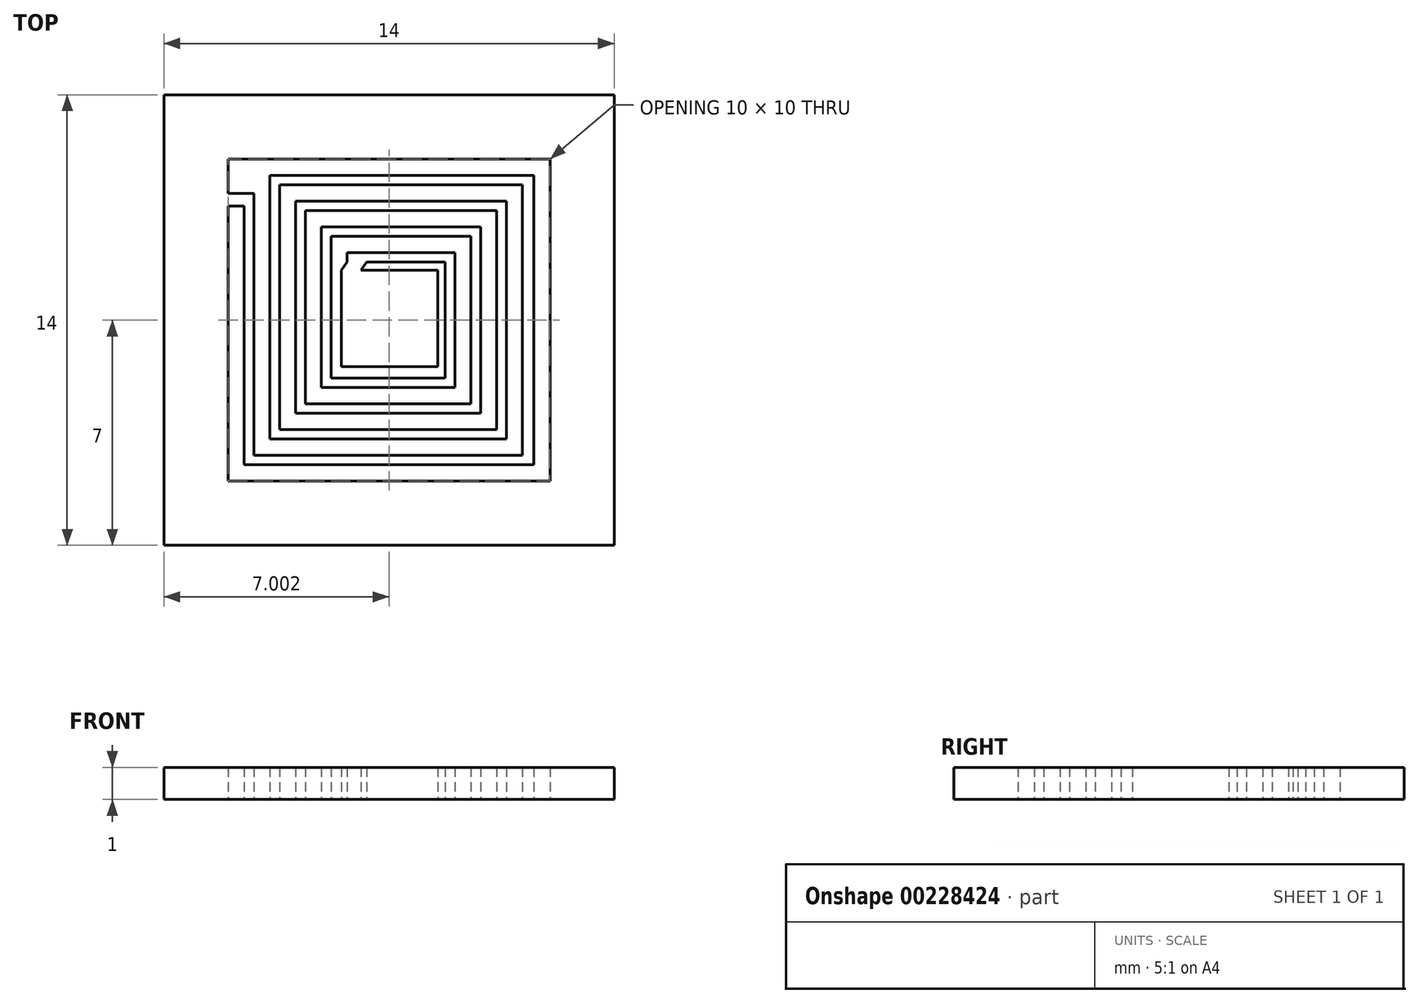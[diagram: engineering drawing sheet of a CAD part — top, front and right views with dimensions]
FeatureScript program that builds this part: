
annotation { "Feature Type Name" : "Feature", "Feature Type Description" : "" }
export const myFeature = defineFeature(function(context is Context, id is Id, definition is map)
    precondition{}
    {
        {
            var Q0;
            Q0=qCreatedBy(makeId("Top.planeOp"),FACE);
            var sketch = newSketch(context, id + "F0", { "sketchPlane" : qUnion([Q0])});
            skLineSegment(sketch, "E0.bottom", {"start": v(-33.55, 10) * mm, "end": v(-23.55, 10) * mm});
            skLineSegment(sketch, "E0.top", {"start": v(-33.55, 0) * mm, "end": v(-23.55, 0) * mm});
            skLineSegment(sketch, "E0.left", {"start": v(-33.55, 10) * mm, "end": v(-33.55, 0) * mm});
            skLineSegment(sketch, "E0.right", {"start": v(-23.55, 10) * mm, "end": v(-23.55, 0) * mm});
            skLineSegment(sketch, "E1.bottom", {"start": v(-29.42, 6.55) * mm, "end": v(-27.03, 6.55) * mm});
            skLineSegment(sketch, "E1.top", {"start": v(-30.03, 3.55) * mm, "end": v(-27.03, 3.55) * mm});
            skLineSegment(sketch, "E1.left", {"start": v(-30.03, 6.55) * mm, "end": v(-30.03, 3.55) * mm});
            skLineSegment(sketch, "E1.right", {"start": v(-27.03, 6.55) * mm, "end": v(-27.03, 3.55) * mm});
            skLineSegment(sketch, "E2.bottom", {"start": v(-33.05, 8.94) * mm, "end": v(-32.75, 8.94) * mm});
            skLineSegment(sketch, "E2.left", {"start": v(-33.05, 8.54) * mm, "end": v(-33.05, 0.8) * mm});
            skLineSegment(sketch, "E2.right", {"start": v(-32.75, 8.94) * mm, "end": v(-32.75, 0.8) * mm});
            skLineSegment(sketch, "E3", {"start": v(-33.05, 8.94) * mm, "end": v(-33.55, 8.94) * mm});
            skLineSegment(sketch, "E4", {"start": v(-33.55, 8.54) * mm, "end": v(-33.05, 8.54) * mm});
            skLineSegment(sketch, "E5.bottom", {"start": v(-32.75, 0.8) * mm, "end": v(-24.4, 0.8) * mm});
            skLineSegment(sketch, "E5.top", {"start": v(-33.05, 0.5) * mm, "end": v(-24.05, 0.5) * mm});
            skLineSegment(sketch, "E5.left", {"start": v(-33.05, 0.8) * mm, "end": v(-33.05, 0.5) * mm});
            skLineSegment(sketch, "E5.right", {"start": v(-24.05, 0.8) * mm, "end": v(-24.05, 0.5) * mm});
            skLineSegment(sketch, "E6.top", {"start": v(-24.05, 9.5) * mm, "end": v(-24.4, 9.5) * mm});
            skLineSegment(sketch, "E6.left", {"start": v(-24.05, 0.8) * mm, "end": v(-24.05, 9.5) * mm});
            skLineSegment(sketch, "E6.right", {"start": v(-24.4, 0.8) * mm, "end": v(-24.4, 9.2) * mm});
            skLineSegment(sketch, "E7.bottom", {"start": v(-24.4, 9.5) * mm, "end": v(-32.25, 9.5) * mm});
            skLineSegment(sketch, "E7.top", {"start": v(-24.4, 9.2) * mm, "end": v(-31.95, 9.2) * mm});
            skLineSegment(sketch, "E7.right", {"start": v(-32.25, 9.5) * mm, "end": v(-32.25, 9.2) * mm});
            skLineSegment(sketch, "E8.top", {"start": v(-32.25, 1.3) * mm, "end": v(-31.95, 1.3) * mm});
            skLineSegment(sketch, "E8.left", {"start": v(-32.25, 9.2) * mm, "end": v(-32.25, 1.3) * mm});
            skLineSegment(sketch, "E8.right", {"start": v(-31.95, 9.2) * mm, "end": v(-31.95, 1.6) * mm});
            skLineSegment(sketch, "E9.bottom", {"start": v(-31.95, 1.3) * mm, "end": v(-24.9, 1.3) * mm});
            skLineSegment(sketch, "E9.top", {"start": v(-31.95, 1.6) * mm, "end": v(-25.2, 1.6) * mm});
            skLineSegment(sketch, "E9.right", {"start": v(-24.9, 1.3) * mm, "end": v(-24.9, 1.6) * mm});
            skLineSegment(sketch, "E10.top", {"start": v(-24.9, 8.7) * mm, "end": v(-25.2, 8.7) * mm});
            skLineSegment(sketch, "E10.left", {"start": v(-24.9, 1.6) * mm, "end": v(-24.9, 8.7) * mm});
            skLineSegment(sketch, "E10.right", {"start": v(-25.2, 1.6) * mm, "end": v(-25.2, 8.4) * mm});
            skLineSegment(sketch, "E11.bottom", {"start": v(-25.2, 8.7) * mm, "end": v(-31.45, 8.7) * mm});
            skLineSegment(sketch, "E11.top", {"start": v(-25.2, 8.4) * mm, "end": v(-31.15, 8.4) * mm});
            skLineSegment(sketch, "E11.right", {"start": v(-31.45, 8.7) * mm, "end": v(-31.45, 8.4) * mm});
            skLineSegment(sketch, "E12.top", {"start": v(-31.45, 2.1) * mm, "end": v(-31.15, 2.1) * mm});
            skLineSegment(sketch, "E12.left", {"start": v(-31.45, 8.4) * mm, "end": v(-31.45, 2.1) * mm});
            skLineSegment(sketch, "E12.right", {"start": v(-31.15, 8.4) * mm, "end": v(-31.15, 2.4) * mm});
            skLineSegment(sketch, "E13.bottom", {"start": v(-31.15, 2.1) * mm, "end": v(-25.7, 2.1) * mm});
            skLineSegment(sketch, "E13.top", {"start": v(-31.15, 2.4) * mm, "end": v(-26, 2.4) * mm});
            skLineSegment(sketch, "E13.right", {"start": v(-25.7, 2.1) * mm, "end": v(-25.7, 2.4) * mm});
            skLineSegment(sketch, "E14.top", {"start": v(-25.7, 7.9) * mm, "end": v(-26, 7.9) * mm});
            skLineSegment(sketch, "E14.left", {"start": v(-25.7, 2.4) * mm, "end": v(-25.7, 7.9) * mm});
            skLineSegment(sketch, "E14.right", {"start": v(-26, 2.4) * mm, "end": v(-26, 7.6) * mm});
            skLineSegment(sketch, "E15.bottom", {"start": v(-26, 7.9) * mm, "end": v(-30.65, 7.9) * mm});
            skLineSegment(sketch, "E15.top", {"start": v(-26, 7.6) * mm, "end": v(-30.35, 7.6) * mm});
            skLineSegment(sketch, "E15.right", {"start": v(-30.65, 7.9) * mm, "end": v(-30.65, 7.6) * mm});
            skLineSegment(sketch, "E16.top", {"start": v(-30.65, 2.9) * mm, "end": v(-30.35, 2.9) * mm});
            skLineSegment(sketch, "E16.left", {"start": v(-30.65, 7.6) * mm, "end": v(-30.65, 2.9) * mm});
            skLineSegment(sketch, "E16.right", {"start": v(-30.35, 7.6) * mm, "end": v(-30.35, 3.2) * mm});
            skLineSegment(sketch, "E17.bottom", {"start": v(-30.35, 2.9) * mm, "end": v(-26.5, 2.9) * mm});
            skLineSegment(sketch, "E17.top", {"start": v(-30.35, 3.2) * mm, "end": v(-26.8, 3.2) * mm});
            skLineSegment(sketch, "E17.right", {"start": v(-26.5, 2.9) * mm, "end": v(-26.5, 3.2) * mm});
            skLineSegment(sketch, "E18.top", {"start": v(-26.5, 7.1) * mm, "end": v(-26.8, 7.1) * mm});
            skLineSegment(sketch, "E18.left", {"start": v(-26.5, 3.2) * mm, "end": v(-26.5, 7.1) * mm});
            skLineSegment(sketch, "E18.right", {"start": v(-26.8, 3.2) * mm, "end": v(-26.8, 6.8) * mm});
            skLineSegment(sketch, "E19.bottom", {"start": v(-26.8, 7.1) * mm, "end": v(-29.85, 7.1) * mm});
            skLineSegment(sketch, "E19.top", {"start": v(-26.8, 6.8) * mm, "end": v(-29.25, 6.8) * mm});
            skLineSegment(sketch, "E19.right", {"start": v(-29.85, 7.1) * mm, "end": v(-29.85, 6.8) * mm});
            skLineSegment(sketch, "E20", {"start": v(-29.85, 6.8) * mm, "end": v(-30.03, 6.55) * mm});
            skLineSegment(sketch, "E21", {"start": v(-29.25, 6.8) * mm, "end": v(-29.42, 6.55) * mm});
            skLineSegment(sketch, "E22.bottom", {"start": v(-35.55, 12) * mm, "end": v(-21.55, 12) * mm});
            skLineSegment(sketch, "E22.top", {"start": v(-35.55, -2) * mm, "end": v(-21.55, -2) * mm});
            skLineSegment(sketch, "E22.left", {"start": v(-35.55, 12) * mm, "end": v(-35.55, -2) * mm});
            skLineSegment(sketch, "E22.right", {"start": v(-21.55, 12) * mm, "end": v(-21.55, -2) * mm});
            skSolve(sketch);
        }
        {
            var Q0;
            {var subQ3=sQuery(id+"F0.wireOp",EDGE,"E0.bottom");Q0=makeQuery(id+"F0.imprint","IMPRINT",FACE,{"disambiguationData":[TD([[makeQuery(id+"F0.imprint","IMPRINT",EDGE,{"derivedFrom":subQ3}),1.0]])]});}
            var Q1;
            Q1=makeQuery(id+"F0.imprint","IMPRINT",FACE,{"disambiguationData":[TD([[makeQuery(id+"F0.imprint","IMPRINT",EDGE,{"derivedFrom":sQuery(id+"F0.wireOp",EDGE,"E1.bottom")}),-1.0]])]});
            extrude(context, id + "F1", {"entities" : qUnion([Q0, Q1]), "depth" : 1 * mm});
        }
    });
